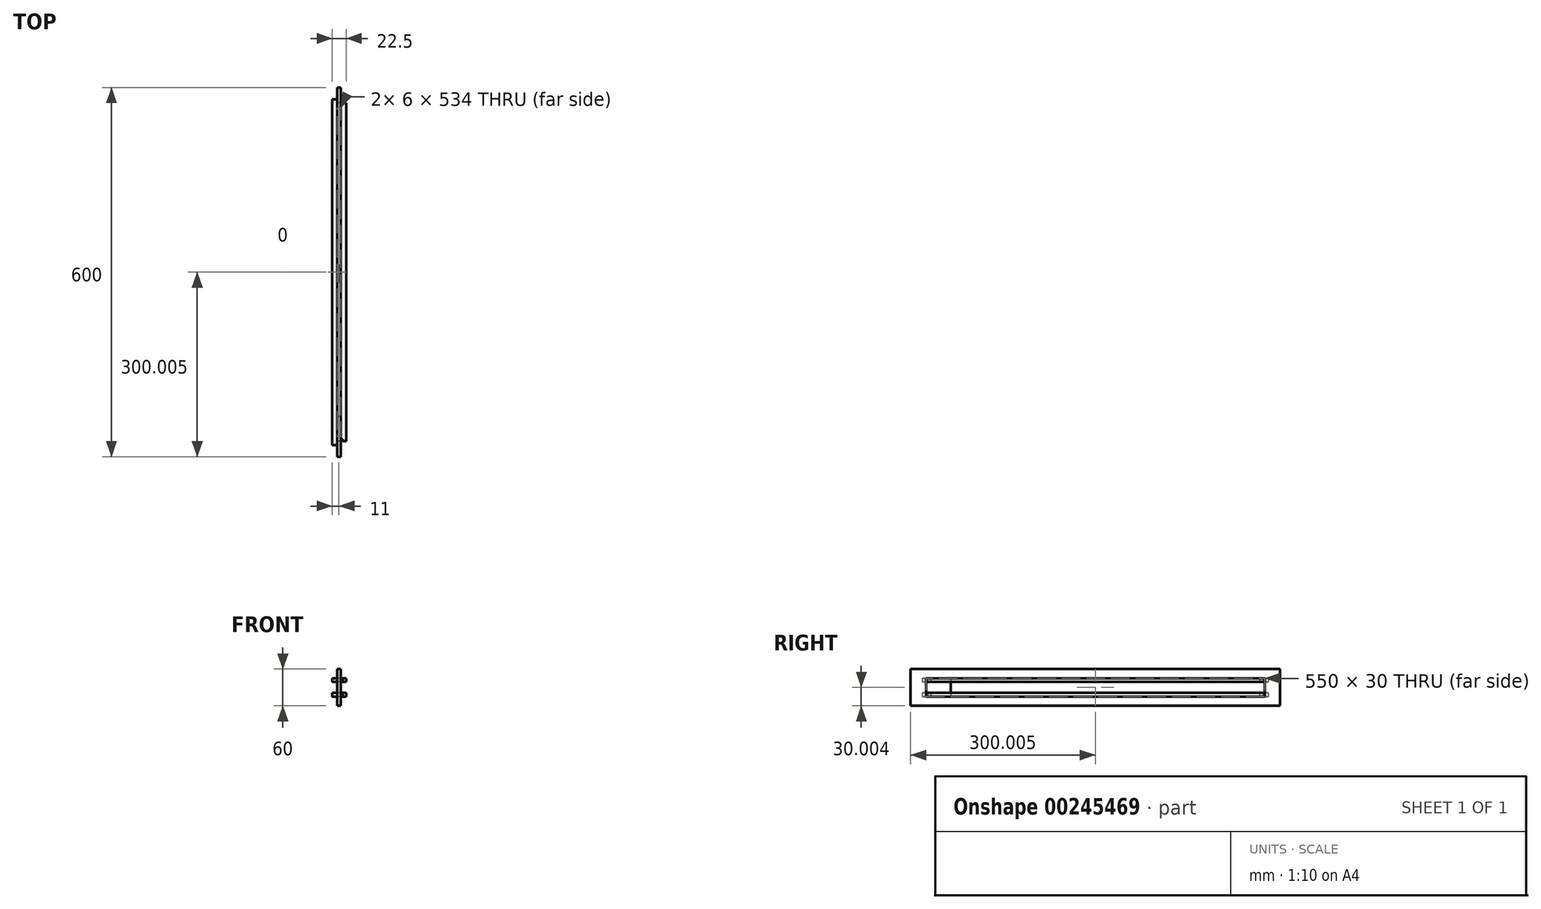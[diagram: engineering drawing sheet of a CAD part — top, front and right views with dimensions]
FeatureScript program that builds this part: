
annotation { "Feature Type Name" : "Feature", "Feature Type Description" : "" }
export const myFeature = defineFeature(function(context is Context, id is Id, definition is map)
    precondition{}
    {
        {
            assignVariable(context, id + "F0", {"name" : "slide_thick", "anyValue" : 6});
        }
        {
            var Q0;
            Q0=qCreatedBy(makeId("Right.planeOp"),FACE);
            var sketch = newSketch(context, id + "F1", { "sketchPlane" : qUnion([Q0])});
            skLineSegment(sketch, "E0", {"start": v(-297.37, -65.03) * mm, "end": v(-297.37, -5.03) * mm});
            skLineSegment(sketch, "E1", {"start": v(-297.37, -5.03) * mm, "end": v(302.63, -5.03) * mm});
            skLineSegment(sketch, "E2", {"start": v(302.63, -5.03) * mm, "end": v(302.63, -65.03) * mm});
            skLineSegment(sketch, "E3", {"start": v(302.63, -65.03) * mm, "end": v(-297.37, -65.03) * mm});
            skLineSegment(sketch, "E4", {"start": v(-272.37, -20.03) * mm, "end": v(-272.37, -50.03) * mm});
            skLineSegment(sketch, "E5", {"start": v(-272.37, -50.03) * mm, "end": v(277.63, -50.03) * mm});
            skLineSegment(sketch, "E6", {"start": v(277.63, -50.03) * mm, "end": v(277.63, -20.03) * mm});
            skLineSegment(sketch, "E7", {"start": v(277.63, -20.03) * mm, "end": v(-272.37, -20.03) * mm});
            skSolve(sketch);
        }
        {
            var Q0;
            Q0 = qSketchRegion(id + "F1", true);
            extrude(context, id + "F2", {"entities" : qUnion([Q0]), "depth" : (getVariable(context, 'slide_thick')) * mm});
        }
        {
            assignVariable(context, id + "F3", {"name" : "block_thick", "anyValue" : 6});
        }
        {
            var Q0;
            Q0=qCreatedBy(makeId("Right.planeOp"),FACE);
            var sketch = newSketch(context, id + "F4", { "sketchPlane" : qUnion([Q0])});
            skLineSegment(sketch, "E8.0", {"start": v(-232.37, -20.03) * mm, "end": v(-272.37, -20.03) * mm});
            skLineSegment(sketch, "E9.0", {"start": v(-272.37, -50.03) * mm, "end": v(-232.37, -50.03) * mm});
            skLineSegment(sketch, "E10", {"start": v(-232.37, -20.03) * mm, "end": v(-232.37, -50.03) * mm});
            skPoint(sketch, "E11.orphan", {"position": v(277.63, -20.03) * mm});
            skPoint(sketch, "E12.orphan", {"position": v(277.63, -50.03) * mm});
            skLineSegment(sketch, "E13", {"start": v(-272.37, -20.03) * mm, "end": v(-272.37, -50.03) * mm});
            skSolve(sketch);
        }
        {
            var Q0;
            Q0=makeQuery(id+"F4.imprint","IMPRINT",FACE,{"disambiguationData":[TD([[makeQuery(id+"F4.imprint","IMPRINT",EDGE,{"derivedFrom":sQuery(id+"F4.wireOp",EDGE,"E8.0")}),1.0]])]});
            extrude(context, id + "F5", {"entities" : qUnion([Q0]), "depth" : (getVariable(context, 'block_thick')) * mm});
        }
        {
            var Q0;
            Q0=makeQuery(id+"F2.opExtrude","SWEPT_FACE",FACE,{"disambiguationData":[OSD([sQuery(id+"F1.wireOp",EDGE,"E5")])]});
            var sketch = newSketch(context, id + "F6", { "sketchPlane" : qUnion([Q0])});
            skLineSegment(sketch, "E14.0", {"start": v(6, 269.63) * mm, "end": v(6, -264.37) * mm});
            skLineSegment(sketch, "E15.0", {"start": v(0, 269.63) * mm, "end": v(0, -264.37) * mm});
            skPoint(sketch, "E16.orphan", {"position": v(0, -232.37) * mm});
            skLineSegment(sketch, "E17", {"start": v(0, 277.63) * mm, "end": v(0, 283.63) * mm});
            skLineSegment(sketch, "E18", {"start": v(0, 283.63) * mm, "end": v(-8, 283.63) * mm});
            skLineSegment(sketch, "E19", {"start": v(-8, 283.63) * mm, "end": v(-8, -272.37) * mm});
            skLineSegment(sketch, "E20", {"start": v(-8, -272.37) * mm, "end": v(-8, -278.37) * mm});
            skLineSegment(sketch, "E21", {"start": v(-8, -278.37) * mm, "end": v(0, -278.37) * mm});
            skLineSegment(sketch, "E22", {"start": v(0, -278.37) * mm, "end": v(0, -272.37) * mm});
            skLineSegment(sketch, "E23", {"start": v(14.5, -272.37) * mm, "end": v(14.5, 277.63) * mm});
            skLineSegment(sketch, "E24", {"start": v(6, -264.37) * mm, "end": v(0, -264.37) * mm});
            skLineSegment(sketch, "E25", {"start": v(6, 269.63) * mm, "end": v(0, 269.63) * mm});
            skPoint(sketch, "E26.start.orphan", {"position": v(9, 277.63) * mm});
            skPoint(sketch, "E27.0.start.orphan", {"position": v(6, 277.63) * mm});
            skLineSegment(sketch, "E28.0", {"start": v(6, 277.63) * mm, "end": v(0, 277.63) * mm});
            skLineSegment(sketch, "E29.0", {"start": v(6, -272.37) * mm, "end": v(0, -272.37) * mm});
            skLineSegment(sketch, "E30", {"start": v(6, 277.63) * mm, "end": v(6, 274.63) * mm});
            skLineSegment(sketch, "E31", {"start": v(6, 274.63) * mm, "end": v(9, 274.63) * mm});
            skLineSegment(sketch, "E32", {"start": v(9, 274.63) * mm, "end": v(9, 277.63) * mm});
            skLineSegment(sketch, "E33", {"start": v(9, 277.63) * mm, "end": v(14.5, 277.63) * mm});
            skPoint(sketch, "E34.start.orphan", {"position": v(9, -272.37) * mm});
            skPoint(sketch, "E35.start.orphan", {"position": v(9, -278.37) * mm});
            skLineSegment(sketch, "E36", {"start": v(6, -272.37) * mm, "end": v(6, -269.37) * mm});
            skLineSegment(sketch, "E37", {"start": v(6, -269.37) * mm, "end": v(9, -269.37) * mm});
            skLineSegment(sketch, "E38", {"start": v(9, -269.37) * mm, "end": v(9, -272.37) * mm});
            skLineSegment(sketch, "E39", {"start": v(9, -272.37) * mm, "end": v(14.5, -272.37) * mm});
            skSolve(sketch);
        }
        {
            var Q0;
            Q0 = qSketchRegion(id + "F6", true);
            extrude(context, id + "F7", {"entities" : qUnion([Q0]), "depth" : 6 * mm});
        }
        {
            var Q0;
            Q0=makeQuery(id+"F7.opExtrude","SWEPT_BODY",BODY,{"disambiguationData":[OSD([sQuery(id+"F6.wireOp",EDGE,"E14.0"),sQuery(id+"F6.wireOp",EDGE,"E15.0"),sQuery(id+"F6.wireOp",EDGE,"E17"),sQuery(id+"F6.wireOp",EDGE,"E18"),sQuery(id+"F6.wireOp",EDGE,"E19"),sQuery(id+"F6.wireOp",EDGE,"E20"),sQuery(id+"F6.wireOp",EDGE,"E21"),sQuery(id+"F6.wireOp",EDGE,"E22"),sQuery(id+"F6.wireOp",EDGE,"E23"),sQuery(id+"F6.wireOp",EDGE,"E24"),sQuery(id+"F6.wireOp",EDGE,"E25"),sQuery(id+"F6.wireOp",EDGE,"E28.0"),sQuery(id+"F6.wireOp",EDGE,"E29.0"),sQuery(id+"F6.wireOp",EDGE,"E30"),sQuery(id+"F6.wireOp",EDGE,"E31"),sQuery(id+"F6.wireOp",EDGE,"E32"),sQuery(id+"F6.wireOp",EDGE,"E33"),sQuery(id+"F6.wireOp",EDGE,"E36"),sQuery(id+"F6.wireOp",EDGE,"E37"),sQuery(id+"F6.wireOp",EDGE,"E38"),sQuery(id+"F6.wireOp",EDGE,"E39")])]});
            transform(context, id + "F8", {"entities" : qUnion([Q0]), "transformType" : TransformType.TRANSLATION_3D, "dx" : 0 * mm, "dy" : 0 * mm, "dz" : 24 * mm, "makeCopy" : true});
        }
    });
